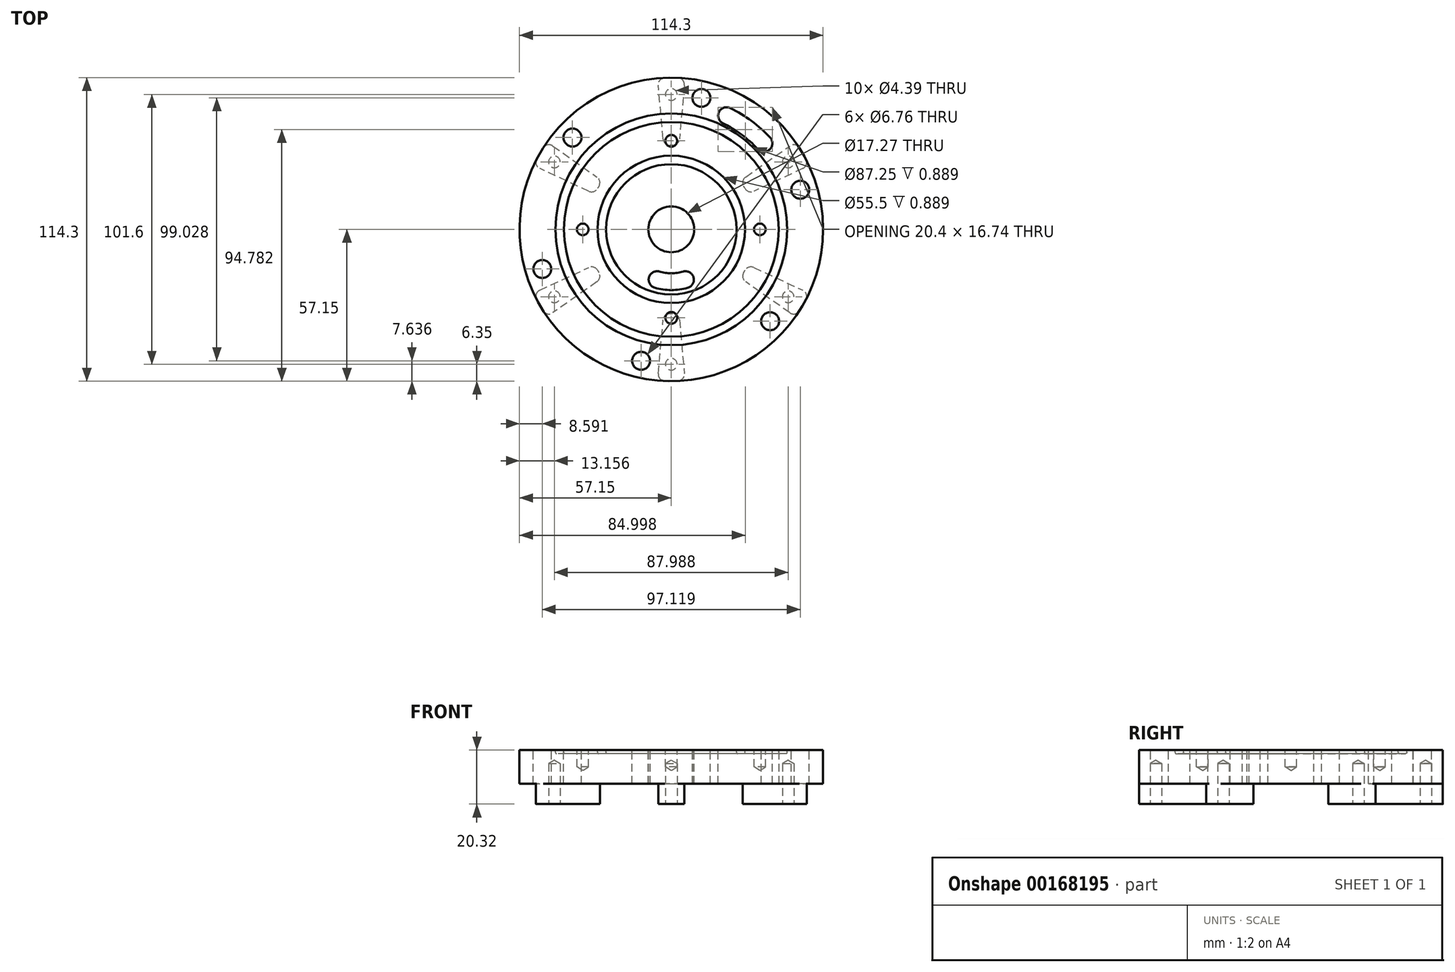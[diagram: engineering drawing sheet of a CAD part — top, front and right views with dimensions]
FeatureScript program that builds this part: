
annotation { "Feature Type Name" : "Feature", "Feature Type Description" : "" }
export const myFeature = defineFeature(function(context is Context, id is Id, definition is map)
    precondition{}
    {
        {
            var Q0;
            Q0=qCreatedBy(makeId("Top.planeOp"),FACE);
            var sketch = newSketch(context, id + "F0", { "sketchPlane" : qUnion([Q0])});
            skCircle(sketch, "E0", {"center": v(0, 0) * mm, "radius": 57.15 * mm});
            skSolve(sketch);
        }
        {
            var Q0;
            Q0=makeQuery(id+"F0.imprint","IMPRINT",FACE,{"disambiguationData":[TD([[makeQuery(id+"F0.imprint","IMPRINT",EDGE,{"derivedFrom":sQuery(id+"F0.wireOp",EDGE,"E0")}),1.0]])]});
            extrude(context, id + "F1", {"entities" : qUnion([Q0]), "depth" : 12.7 * mm});
        }
        {
            var Q0;
            Q0=makeQuery(id+"FNZgXB3MDCEPfWC_1.boolean.opBoolean","SPLIT",FACE,{"disambiguationData":[TD([makeQuery(id+"FNZgXB3MDCEPfWC_1.opExtrude","SWEPT_FACE",FACE,{"disambiguationData":[OSD([sQuery(id+"FiLk9hSRQ8Dv81E_1.wireOp",EDGE,"Xvq2NHEn-EDZK-GzOR-rNrk-moL4fFsD4KvI")])]})])],"derivedFrom":makeQuery(id+"F1.opExtrude","CAP_FACE",FACE,{"disambiguationData":[OSD([sQuery(id+"F0.wireOp",EDGE,"E0")])],"isStart":false})});
            var sketch = newSketch(context, id + "F2", { "sketchPlane" : qUnion([Q0])});
            skCircle(sketch, "E1", {"center": v(0, 0) * mm, "radius": 8.64 * mm});
            skSolve(sketch);
        }
        {
            var Q0;
            Q0=qSketchRegion(id+"F2",true);
            extrude(context, id + "F3", {"entities" : qUnion([Q0]), "operationType" : NewBodyOperationType.REMOVE, "endBound" : BoundingType.THROUGH_ALL, "oppositeDirection" : true, "depth" : 25.4 * mm});
        }
        {
            var Q0;
            Q0=makeQuery(id+"F1.opExtrude","CAP_FACE",FACE,{"disambiguationData":[OSD([sQuery(id+"F0.wireOp",EDGE,"E0")])],"isStart":true});
            var sketch = newSketch(context, id + "F4", { "sketchPlane" : qUnion([Q0])});
            skArc(sketch, "E2", {"start": v(-5.14, -56.92) * mm, "mid": v(0, -57.15) * mm, "end": v(5.14, -56.92) * mm});
            skArc(sketch, "E3", {"start": v(-2.86, -31.62) * mm, "mid": v(0, -31.75) * mm, "end": v(2.86, -31.62) * mm});
            skLineSegment(sketch, "E4", {"start": v(0, 0) * mm, "end": v(2.86, -31.62) * mm, "construction": true});
            skLineSegment(sketch, "E5", {"start": v(5.14, -56.92) * mm, "end": v(2.86, -31.62) * mm});
            skLineSegment(sketch, "E6", {"start": v(-2.86, -31.62) * mm, "end": v(-5.14, -56.92) * mm});
            skLineSegment(sketch, "E7", {"start": v(-2.86, -31.62) * mm, "end": v(2.86, -31.62) * mm, "construction": true});
            skPoint(sketch, "E8", {"position": v(0, -31.62) * mm});
            skLineSegment(sketch, "E9", {"start": v(0, 0) * mm, "end": v(-2.86, -31.62) * mm, "construction": true});
            skSolve(sketch);
        }
        {
            var Q0;
            Q0=qSketchRegion(id+"F4",true);
            extrude(context, id + "F5", {"entities" : qUnion([Q0]), "operationType" : NewBodyOperationType.ADD, "depth" : 7.62 * mm});
        }
        {
            var Q0;
            Q0=makeQuery(id+"F5.opExtrude","SWEPT_EDGE",EDGE,{"disambiguationData":[OSD([sQuery(id+"F0.wireOp",EDGE,"E0"),sQuery(id+"F4.wireOp",EDGE,"E2"),sQuery(id+"F4.wireOp",EDGE,"E5")])]});
            var Q1;
            Q1=makeQuery(id+"F5.opExtrude","SWEPT_EDGE",EDGE,{"disambiguationData":[OSD([sQuery(id+"F4.wireOp",EDGE,"E3"),sQuery(id+"F4.wireOp",EDGE,"E5")])]});
            var Q2;
            Q2=makeQuery(id+"F5.opExtrude","SWEPT_EDGE",EDGE,{"disambiguationData":[OSD([sQuery(id+"F0.wireOp",EDGE,"E0"),sQuery(id+"F4.wireOp",EDGE,"E2"),sQuery(id+"F4.wireOp",EDGE,"sxsrdx0H-xiQs-OsdF-6Z6r-2XBd8uqwUAgb")])]});
            var Q3;
            Q3=makeQuery(id+"F5.opExtrude","SWEPT_EDGE",EDGE,{"disambiguationData":[OSD([sQuery(id+"F4.wireOp",EDGE,"E3"),sQuery(id+"F4.wireOp",EDGE,"sxsrdx0H-xiQs-OsdF-6Z6r-2XBd8uqwUAgb")])]});
            fillet(context, id + "F6", {"entities" : qUnion([Q0, Q1, Q2, Q3]), "radius" : 2.54 * mm, "tangentPropagation" : true, "allowEdgeOverflow" : false});
        }
        {
            var Q0;
            Q0=makeQuery(id+"F5.opExtrude","CAP_FACE",FACE,{"disambiguationData":[OSD([sQuery(id+"F4.wireOp",EDGE,"E2"),sQuery(id+"F4.wireOp",EDGE,"E3"),sQuery(id+"F4.wireOp",EDGE,"E5"),sQuery(id+"F4.wireOp",EDGE,"sxsrdx0H-xiQs-OsdF-6Z6r-2XBd8uqwUAgb")])],"isStart":false});
            var sketch = newSketch(context, id + "F7", { "sketchPlane" : qUnion([Q0])});
            skPoint(sketch, "E10", {"position": v(0, -17.36) * mm});
            skLineSegment(sketch, "E11", {"start": v(0, 0) * mm, "end": v(0, -17.36) * mm, "construction": true});
            skLineSegment(sketch, "E12", {"start": v(0, -17.36) * mm, "end": v(0, -57.1) * mm, "construction": true});
            skPoint(sketch, "E13.3.0", {"position": v(0, -50.8) * mm});
            skPoint(sketch, "E13.center", {"position": v(0, 0) * mm});
            skPoint(sketch, "E14.1.0", {"position": v(44, -25.4) * mm});
            skPoint(sketch, "E14.2.0", {"position": v(44, 25.4) * mm});
            skPoint(sketch, "E15.0.3.0", {"position": v(0, 50.8) * mm});
            skPoint(sketch, "E15.0.4.0", {"position": v(-44, 25.4) * mm});
            skPoint(sketch, "E15.0.5.0", {"position": v(-44, -25.4) * mm});
            skSolve(sketch);
        }
        {
            var Q0;
            Q0=makeQuery(id+"F1.opExtrude","SWEPT_BODY",BODY,{"disambiguationData":[OSD([sQuery(id+"F0.wireOp",EDGE,"E0")])]});
            var Q1;
            Q1=makeQuery(id+"F3.boolean.opBoolean","COPY",FACE,{"derivedFrom":makeQuery(id+"F3.opExtrude","SWEPT_FACE",FACE,{"disambiguationData":[OSD([sQuery(id+"F2.wireOp",EDGE,"E1")])]})});
            circularPattern(context, id + "F8", {"operationType" : NewBodyOperationType.ADD, "entities" : qUnion([Q0]), "axis" : qUnion([Q1]), "angle" : 360 * degree, "instanceCount" : 6, "equalSpace" : true});
        }
        {
            var Q0;
            Q0=sQuery(id+"F7.wireOp",VERTEX,"E13.3.0");
            var Q1;
            Q1=sQuery(id+"F7.wireOp",VERTEX,"E14.1.0");
            var Q2;
            Q2=sQuery(id+"F7.wireOp",VERTEX,"E14.2.0");
            var Q3;
            Q3=sQuery(id+"F7.wireOp",VERTEX,"E15.0.3.0");
            var Q4;
            Q4=sQuery(id+"F7.wireOp",VERTEX,"E15.0.4.0");
            var Q5;
            Q5=sQuery(id+"F7.wireOp",VERTEX,"E15.0.5.0");
            var Q6;
            Q6=makeQuery(id+"F1.opExtrude","SWEPT_BODY",BODY,{"disambiguationData":[OSD([sQuery(id+"F0.wireOp",EDGE,"E0")])]});
            hole(context, id + "F9", {"style" : HoleStyle.SIMPLE, "endStyle" : HoleEndStyle.BLIND, "holeDiameter" : 4.4 * mm, "holeDepth" : 15.24 * mm, "locations" : qUnion([Q0, Q1, Q2, Q3, Q4, Q5]), "scope" : qUnion([Q6])});
        }
        {
            var Q0;
            {var subQ0=sQuery(id+"F0.wireOp",EDGE,"E0");Q0=makeQuery(id+"FNZgXB3MDCEPfWC_1.boolean.opBoolean","SPLIT",FACE,{"disambiguationData":[TD([makeQuery(id+"F1.opExtrude","SWEPT_FACE",FACE,{"disambiguationData":[OSD([subQ0])]})])],"derivedFrom":makeQuery(id+"F1.opExtrude","CAP_FACE",FACE,{"disambiguationData":[OSD([subQ0])],"isStart":false})});}
            var sketch = newSketch(context, id + "F10", { "sketchPlane" : qUnion([Q0])});
            skCircle(sketch, "E16", {"center": v(0, 0) * mm, "radius": 42.02 * mm, "construction": true});
            skCircle(sketch, "E17", {"center": v(0, 0) * mm, "radius": 40.42 * mm});
            skCircle(sketch, "E18", {"center": v(0, 0) * mm, "radius": 43.62 * mm});
            skSolve(sketch);
        }
        {
            var Q0;
            Q0=qSketchRegion(id+"F10",true);
            extrude(context, id + "F11", {"entities" : qUnion([Q0]), "operationType" : NewBodyOperationType.REMOVE, "oppositeDirection" : true, "depth" : 1.3 * mm});
        }
        {
            var Q0;
            Q0=makeQuery(id+"F11.boolean.opBoolean","COPY",EDGE,{"derivedFrom":makeQuery(id+"F11.opExtrude","CAP_EDGE",EDGE,{"disambiguationData":[OSD([sQuery(id+"F10.wireOp",EDGE,"E18")])],"isStart":false})});
            var Q1;
            Q1=makeQuery(id+"F11.boolean.opBoolean","COPY",EDGE,{"derivedFrom":makeQuery(id+"F11.opExtrude","CAP_EDGE",EDGE,{"disambiguationData":[OSD([sQuery(id+"F10.wireOp",EDGE,"E17")])],"isStart":false})});
            fillet(context, id + "F12", {"entities" : qUnion([Q0, Q1]), "radius" : 0.4 * mm, "tangentPropagation" : true, "allowEdgeOverflow" : false});
        }
        {
            var Q0;
            {var subQ0=sQuery(id+"F0.wireOp",EDGE,"E0");var subQ1=makeQuery(id+"F1.opExtrude","SWEPT_FACE",FACE,{"disambiguationData":[OSD([subQ0])]});Q0=makeQuery(id+"F11.boolean.opBoolean","SPLIT",FACE,{"disambiguationData":[TD([subQ1])],"derivedFrom":makeQuery(id+"FNZgXB3MDCEPfWC_1.boolean.opBoolean","SPLIT",FACE,{"disambiguationData":[TD([subQ1])],"derivedFrom":makeQuery(id+"F1.opExtrude","CAP_FACE",FACE,{"disambiguationData":[OSD([subQ0])],"isStart":false})})});}
            var sketch = newSketch(context, id + "F13", { "sketchPlane" : qUnion([Q0])});
            skArc(sketch, "E19", {"start": v(33.85, 27.51) * mm, "mid": v(25.95, 35.07) * mm, "end": v(16.41, 40.42) * mm, "construction": true});
            skArc(sketch, "E20.0", {"start": v(34.5, 28.03) * mm, "mid": v(26.44, 35.73) * mm, "end": v(16.72, 41.19) * mm});
            skArc(sketch, "E21", {"start": v(39.42, 32.04) * mm, "mid": v(30.22, 40.84) * mm, "end": v(19.1, 47.07) * mm});
            skLineSegment(sketch, "E22", {"start": v(33.85, 27.51) * mm, "end": v(34.5, 28.03) * mm, "construction": true});
            skLineSegment(sketch, "E23", {"start": v(39.42, 32.04) * mm, "end": v(34.5, 28.03) * mm});
            skLineSegment(sketch, "E24", {"start": v(0, 0) * mm, "end": v(33.85, 27.51) * mm, "construction": true});
            skLineSegment(sketch, "E25", {"start": v(16.41, 40.42) * mm, "end": v(16.72, 41.19) * mm, "construction": true});
            skLineSegment(sketch, "E26", {"start": v(19.1, 47.07) * mm, "end": v(16.72, 41.19) * mm});
            skLineSegment(sketch, "E27", {"start": v(16.41, 40.42) * mm, "end": v(0, 0) * mm, "construction": true});
            skCircle(sketch, "E28.0", {"center": v(0, 50.8) * mm, "radius": 2.2 * mm, "construction": true});
            skCircle(sketch, "E28.1", {"center": v(44, 25.4) * mm, "radius": 2.2 * mm, "construction": true});
            skLineSegment(sketch, "E29", {"start": v(0, 0) * mm, "end": v(0, 50.8) * mm, "construction": true});
            skLineSegment(sketch, "E30", {"start": v(44, 25.4) * mm, "end": v(0, 0) * mm, "construction": true});
            skSolve(sketch);
        }
        {
            var Q0;
            Q0=qSketchRegion(id+"F13",true);
            extrude(context, id + "F14", {"entities" : qUnion([Q0]), "operationType" : NewBodyOperationType.REMOVE, "endBound" : BoundingType.THROUGH_ALL, "oppositeDirection" : true, "depth" : 25.4 * mm});
        }
        {
            var Q0;
            Q0=makeQuery(id+"F14.boolean.opBoolean","COPY",EDGE,{"derivedFrom":makeQuery(id+"F14.opExtrude","SWEPT_EDGE",EDGE,{"disambiguationData":[OSD([sQuery(id+"F13.wireOp",EDGE,"E21"),sQuery(id+"F13.wireOp",EDGE,"E23")])]})});
            var Q1;
            Q1=makeQuery(id+"F14.boolean.opBoolean","COPY",EDGE,{"derivedFrom":makeQuery(id+"F14.opExtrude","SWEPT_EDGE",EDGE,{"disambiguationData":[OSD([sQuery(id+"F13.wireOp",EDGE,"E21"),sQuery(id+"F13.wireOp",EDGE,"E26")])]})});
            var Q2;
            Q2=makeQuery(id+"F14.boolean.opBoolean","COPY",EDGE,{"derivedFrom":makeQuery(id+"F14.opExtrude","SWEPT_EDGE",EDGE,{"disambiguationData":[OSD([sQuery(id+"F13.wireOp",EDGE,"E20.0"),sQuery(id+"F13.wireOp",EDGE,"E26")])]})});
            var Q3;
            Q3=makeQuery(id+"F14.boolean.opBoolean","COPY",EDGE,{"derivedFrom":makeQuery(id+"F14.opExtrude","SWEPT_EDGE",EDGE,{"disambiguationData":[OSD([sQuery(id+"F13.wireOp",EDGE,"E20.0"),sQuery(id+"F13.wireOp",EDGE,"E23")])]})});
            fillet(context, id + "F15", {"entities" : qUnion([Q0, Q1, Q2, Q3]), "radius" : 3.17 * mm, "tangentPropagation" : true, "allowEdgeOverflow" : false});
        }
        {
            var Q0;
            Q0=makeQuery(id+"F11.boolean.opBoolean","SPLIT",FACE,{"disambiguationData":[TD([makeQuery(id+"F3.boolean.opBoolean","COPY",FACE,{"derivedFrom":makeQuery(id+"F3.opExtrude","SWEPT_FACE",FACE,{"disambiguationData":[OSD([sQuery(id+"F2.wireOp",EDGE,"E1")])]})})])],"derivedFrom":makeQuery(id+"F1.opExtrude","CAP_FACE",FACE,{"disambiguationData":[OSD([sQuery(id+"F0.wireOp",EDGE,"E0")])],"isStart":false})});
            var sketch = newSketch(context, id + "F16", { "sketchPlane" : qUnion([Q0])});
            skCircle(sketch, "E31", {"center": v(0, 0) * mm, "radius": 26.15 * mm, "construction": true});
            skCircle(sketch, "E32", {"center": v(0, 0) * mm, "radius": 24.55 * mm});
            skCircle(sketch, "E33", {"center": v(0, 0) * mm, "radius": 27.75 * mm});
            skSolve(sketch);
        }
        {
            var Q0;
            Q0=qSketchRegion(id+"F16",true);
            extrude(context, id + "F17", {"entities" : qUnion([Q0]), "operationType" : NewBodyOperationType.REMOVE, "oppositeDirection" : true, "depth" : 1.3 * mm});
        }
        {
            var Q0;
            Q0=makeQuery(id+"F17.boolean.opBoolean","COPY",EDGE,{"derivedFrom":makeQuery(id+"F17.opExtrude","CAP_EDGE",EDGE,{"disambiguationData":[OSD([sQuery(id+"F16.wireOp",EDGE,"E33")])],"isStart":false})});
            var Q1;
            Q1=makeQuery(id+"F17.boolean.opBoolean","COPY",EDGE,{"derivedFrom":makeQuery(id+"F17.opExtrude","CAP_EDGE",EDGE,{"disambiguationData":[OSD([sQuery(id+"F16.wireOp",EDGE,"E32")])],"isStart":false})});
            fillet(context, id + "F18", {"entities" : qUnion([Q0, Q1]), "radius" : 0.4 * mm, "tangentPropagation" : true, "allowEdgeOverflow" : false});
        }
        {
            var Q0;
            {var subQ0=makeQuery(id+"F3.boolean.opBoolean","COPY",FACE,{"derivedFrom":makeQuery(id+"F3.opExtrude","SWEPT_FACE",FACE,{"disambiguationData":[OSD([sQuery(id+"F2.wireOp",EDGE,"E1")])]})});Q0=makeQuery(id+"F17.boolean.opBoolean","SPLIT",FACE,{"disambiguationData":[TD([subQ0])],"derivedFrom":makeQuery(id+"F11.boolean.opBoolean","SPLIT",FACE,{"disambiguationData":[TD([subQ0])],"derivedFrom":makeQuery(id+"F1.opExtrude","CAP_FACE",FACE,{"disambiguationData":[OSD([sQuery(id+"F0.wireOp",EDGE,"E0")])],"isStart":false})})});}
            var sketch = newSketch(context, id + "F19", { "sketchPlane" : qUnion([Q0])});
            skLineSegment(sketch, "E34", {"start": v(0, 0) * mm, "end": v(6.98, -14.96) * mm, "construction": true});
            skArc(sketch, "E35", {"start": v(6.98, -14.96) * mm, "mid": v(0, -16.51) * mm, "end": v(-6.98, -14.96) * mm});
            skArc(sketch, "E36", {"start": v(9.66, -20.72) * mm, "mid": v(0, -22.86) * mm, "end": v(-9.66, -20.72) * mm});
            skLineSegment(sketch, "E37", {"start": v(-9.66, -20.72) * mm, "end": v(-6.98, -14.96) * mm});
            skLineSegment(sketch, "E38", {"start": v(0, 0) * mm, "end": v(-6.98, -14.96) * mm, "construction": true});
            skLineSegment(sketch, "E39", {"start": v(9.66, -20.72) * mm, "end": v(6.98, -14.96) * mm});
            skLineSegment(sketch, "E40", {"start": v(0, -16.51) * mm, "end": v(0, 0) * mm, "construction": true});
            skSolve(sketch);
        }
        {
            var Q0;
            Q0=qSketchRegion(id+"F19",true);
            extrude(context, id + "F20", {"entities" : qUnion([Q0]), "operationType" : NewBodyOperationType.REMOVE, "endBound" : BoundingType.THROUGH_ALL, "oppositeDirection" : true, "depth" : 25.4 * mm});
        }
        {
            var Q0;
            Q0=makeQuery(id+"F20.boolean.opBoolean","COPY",EDGE,{"derivedFrom":makeQuery(id+"F20.opExtrude","SWEPT_EDGE",EDGE,{"disambiguationData":[OSD([sQuery(id+"F19.wireOp",EDGE,"E35"),sQuery(id+"F19.wireOp",EDGE,"E37")])]})});
            var Q1;
            Q1=makeQuery(id+"F20.boolean.opBoolean","COPY",EDGE,{"derivedFrom":makeQuery(id+"F20.opExtrude","SWEPT_EDGE",EDGE,{"disambiguationData":[OSD([sQuery(id+"F19.wireOp",EDGE,"E36"),sQuery(id+"F19.wireOp",EDGE,"E37")])]})});
            var Q2;
            Q2=makeQuery(id+"F20.boolean.opBoolean","COPY",EDGE,{"derivedFrom":makeQuery(id+"F20.opExtrude","SWEPT_EDGE",EDGE,{"disambiguationData":[OSD([sQuery(id+"F19.wireOp",EDGE,"E35"),sQuery(id+"F19.wireOp",EDGE,"nJm0js4g-YAOA-XNub-Ppl5-B8IrQimasCNu")])]})});
            var Q3;
            Q3=makeQuery(id+"F20.boolean.opBoolean","COPY",EDGE,{"derivedFrom":makeQuery(id+"F20.opExtrude","SWEPT_EDGE",EDGE,{"disambiguationData":[OSD([sQuery(id+"F19.wireOp",EDGE,"E36"),sQuery(id+"F19.wireOp",EDGE,"nJm0js4g-YAOA-XNub-Ppl5-B8IrQimasCNu")])]})});
            fillet(context, id + "F21", {"entities" : qUnion([Q0, Q1, Q2, Q3]), "radius" : 3.17 * mm, "tangentPropagation" : true, "allowEdgeOverflow" : false});
        }
        {
            var Q0;
            {var subQ0=makeQuery(id+"F11.opExtrude","SWEPT_FACE",FACE,{"disambiguationData":[OSD([sQuery(id+"F10.wireOp",EDGE,"E17")])]});Q0=makeQuery(id+"F17.boolean.opBoolean","SPLIT",FACE,{"disambiguationData":[TD([makeQuery(id+"F11.boolean.opBoolean","COPY",FACE,{"derivedFrom":subQ0})])],"derivedFrom":makeQuery(id+"F11.boolean.opBoolean","SPLIT",FACE,{"disambiguationData":[TD([makeQuery(id+"F3.boolean.opBoolean","COPY",FACE,{"derivedFrom":makeQuery(id+"F3.opExtrude","SWEPT_FACE",FACE,{"disambiguationData":[OSD([sQuery(id+"F2.wireOp",EDGE,"E1")])]})})])],"derivedFrom":makeQuery(id+"F1.opExtrude","CAP_FACE",FACE,{"disambiguationData":[OSD([sQuery(id+"F0.wireOp",EDGE,"E0")])],"isStart":false})})});}
            var sketch = newSketch(context, id + "F22", { "sketchPlane" : qUnion([Q0])});
            skCircle(sketch, "E41", {"center": v(0, 0) * mm, "radius": 33.34 * mm, "construction": true});
            skLineSegment(sketch, "E42", {"start": v(0, 0) * mm, "end": v(0, -33.34) * mm, "construction": true});
            skPoint(sketch, "E43", {"position": v(0, -33.34) * mm});
            skPoint(sketch, "E44", {"position": v(-33.34, 0) * mm});
            skPoint(sketch, "E45", {"position": v(33.34, 0) * mm});
            skPoint(sketch, "E46", {"position": v(0, 33.34) * mm});
            skSolve(sketch);
        }
        {
            var Q0;
            Q0=sQuery(id+"F22.wireOp",VERTEX,"E44");
            var Q1;
            Q1=sQuery(id+"F22.wireOp",VERTEX,"E43");
            var Q2;
            Q2=sQuery(id+"F22.wireOp",VERTEX,"E45");
            var Q3;
            Q3=sQuery(id+"F22.wireOp",VERTEX,"E46");
            var Q4;
            Q4=makeQuery(id+"F1.opExtrude","SWEPT_BODY",BODY,{"disambiguationData":[OSD([sQuery(id+"F0.wireOp",EDGE,"E0")])]});
            hole(context, id + "F23", {"style" : HoleStyle.SIMPLE, "endStyle" : HoleEndStyle.BLIND, "holeDiameter" : 4.4 * mm, "holeDepth" : 6.35 * mm, "locations" : qUnion([Q0, Q1, Q2, Q3]), "scope" : qUnion([Q4])});
        }
        {
            var Q0;
            {var subQ1=sQuery(id+"F0.wireOp",EDGE,"E0");var subQ2=makeQuery(id+"F1.opExtrude","SWEPT_FACE",FACE,{"disambiguationData":[OSD([subQ1])]});Q0=makeQuery(id+"F11.boolean.opBoolean","SPLIT",FACE,{"disambiguationData":[TD([subQ2])],"derivedFrom":makeQuery(id+"F1.opExtrude","CAP_FACE",FACE,{"disambiguationData":[OSD([subQ1])],"isStart":false})});}
            var sketch = newSketch(context, id + "F24", { "sketchPlane" : qUnion([Q0])});
            skLineSegment(sketch, "E47", {"start": v(0, 0) * mm, "end": v(11.36, 49.51) * mm, "construction": true});
            skPoint(sketch, "E48", {"position": v(11.36, 49.51) * mm});
            skPoint(sketch, "E49.1.0", {"position": v(-37.2, 34.6) * mm});
            skPoint(sketch, "E49.2.0", {"position": v(-48.56, -14.92) * mm});
            skPoint(sketch, "E49.3.0", {"position": v(-11.36, -49.51) * mm});
            skPoint(sketch, "E49.4.0", {"position": v(37.2, -34.6) * mm});
            skPoint(sketch, "E49.5.0", {"position": v(48.56, 14.92) * mm});
            skPoint(sketch, "E49.center", {"position": v(0, 0) * mm});
            skSolve(sketch);
        }
        {
            var Q0;
            Q0=sQuery(id+"F24.wireOp",VERTEX,"E48");
            var Q1;
            Q1=sQuery(id+"F24.wireOp",VERTEX,"E49.5.0");
            var Q2;
            Q2=sQuery(id+"F24.wireOp",VERTEX,"E49.4.0");
            var Q3;
            Q3=sQuery(id+"F24.wireOp",VERTEX,"E49.3.0");
            var Q4;
            Q4=sQuery(id+"F24.wireOp",VERTEX,"E49.2.0");
            var Q5;
            Q5=sQuery(id+"F24.wireOp",VERTEX,"E49.1.0");
            var Q6;
            Q6=makeQuery(id+"F1.opExtrude","SWEPT_BODY",BODY,{"disambiguationData":[OSD([sQuery(id+"F0.wireOp",EDGE,"E0")])]});
            hole(context, id + "F25", {"style" : HoleStyle.SIMPLE, "endStyle" : HoleEndStyle.THROUGH, "holeDiameter" : 6.76 * mm, "locations" : qUnion([Q0, Q1, Q2, Q3, Q4, Q5]), "scope" : qUnion([Q6]), "isTappedThrough" : true});
        }
    });
